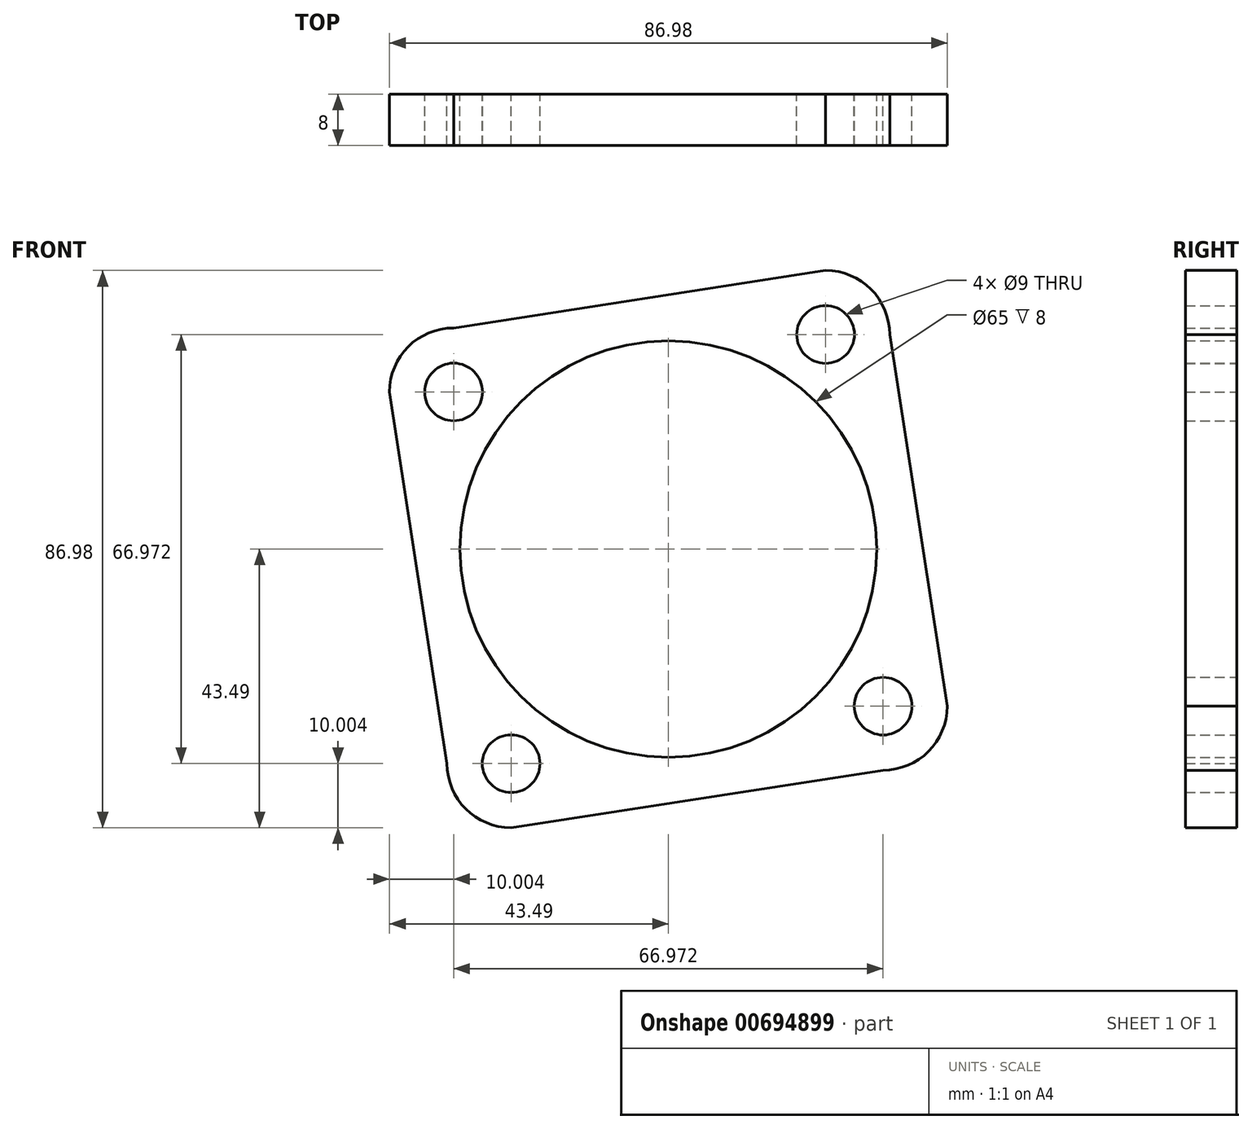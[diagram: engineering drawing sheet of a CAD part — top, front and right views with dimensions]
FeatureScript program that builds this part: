
annotation { "Feature Type Name" : "Feature", "Feature Type Description" : "" }
export const myFeature = defineFeature(function(context is Context, id is Id, definition is map)
    precondition{}
    {
        {
            var Q0;
            Q0=qCreatedBy(makeId("Front.planeOp"),FACE);
            var sketch = newSketch(context, id + "F0", { "sketchPlane" : qUnion([Q0])});
            skCircle(sketch, "E0", {"center": v(0, 0) * mm, "radius": 32.5 * mm});
            skCircle(sketch, "E1", {"center": v(24.51, 33.49) * mm, "radius": 4.5 * mm});
            skCircle(sketch, "E2", {"center": v(-33.49, 24.51) * mm, "radius": 4.5 * mm});
            skCircle(sketch, "E3", {"center": v(-24.51, -33.49) * mm, "radius": 4.5 * mm});
            skCircle(sketch, "E4", {"center": v(33.49, -24.51) * mm, "radius": 4.5 * mm});
            skArc(sketch, "E5", {"start": v(-33.49, 34.51) * mm, "mid": v(-40.56, 31.58) * mm, "end": v(-43.49, 24.51) * mm});
            skArc(sketch, "E6", {"start": v(34.51, 33.49) * mm, "mid": v(31.58, 40.56) * mm, "end": v(24.51, 43.49) * mm});
            skArc(sketch, "E7", {"start": v(33.49, -34.51) * mm, "mid": v(40.56, -31.58) * mm, "end": v(43.49, -24.51) * mm});
            skArc(sketch, "E8", {"start": v(-24.51, -43.49) * mm, "mid": v(-31.58, -40.56) * mm, "end": v(-34.51, -33.49) * mm});
            skLineSegment(sketch, "E9", {"start": v(-33.49, 34.51) * mm, "end": v(24.51, 43.49) * mm});
            skLineSegment(sketch, "E10", {"start": v(34.51, 33.49) * mm, "end": v(43.49, -24.51) * mm});
            skLineSegment(sketch, "E11", {"start": v(33.49, -34.51) * mm, "end": v(-24.51, -43.49) * mm});
            skLineSegment(sketch, "E12", {"start": v(-34.51, -33.49) * mm, "end": v(-43.49, 24.51) * mm});
            skSolve(sketch);
        }
        {
            var Q0;
            Q0 = qSketchRegion(id + "F0", true);
            extrude(context, id + "F1", {"entities" : qUnion([Q0]), "depth" : 8 * mm, "offsetDistance" : 25 * mm});
        }
    });
